# Revit family: PRD_AR_BbChngngUnts_CAMBRINOChangingTable_CAMB10HP_CAMB11HS
name_source: partatom
category: Specialty Equipment
revit_build: Autodesk Revit 2018 (Build: 20190510_1515(x64)
units: mm (PartAtom-declared; Revit-internal decimal feet)

## family parameters
Cut with Voids When Loaded = No
Host = Face
OmniClass Number = 23.40.20.21.37
OmniClass Title = Diaper Changing Units
Part Type = Normal
Room Calculation Point = No
Round Connector Dimension = Use Diameter
Shared = No

## types (2) — shared parameters
AssetType = Fixed
BodyMaterial = PRD_AR_SyntheticWhite
Category = Pr_40_20_76_06, Baby changing units
Color = white
Default Elevation = 900 mm  [stored 2.95276 ft]
DimensionsWhenClosed = 860 x 565 x 100 mm (W x H x D)
DimensionsWhenOpen = 860 x 480 x 570 mm (W x H x D)
DurationUnit = year
Finish = synthetic
Hinged = Yes
IfcExportAs = IfcFurnitureType
IfcExportType = USERDEFINED
IntegralAccessories = incl. mounting materials
IsBuiltIn = TRUE
MainColor = white
Manufacturer = KWC Group AG
ManufacturerName = KWC Group AG
ManufacturerURL = www.kwc.com
Material = synthetic
NBSDescription = Baby changing units
NBSReference = 45-35-72/316
NominalDepth = 100 mm  [stored 0.328084 ft]
NominalHeight = 565 mm  [stored 1.85367 ft]
NominalWidth = 860 mm  [stored 2.82152 ft]
ProductInformation = https://pim.kwc.com
Size = 860 x 565 x 100 mm (W x H x D)
Style = Changing table
TailorMade = No
TypeOfMounting = Wall mounting
URL = www.kwc.com
Uniclass2015Code = Pr_40_20_76_06
Uniclass2015Title = Baby changing units
Uniclass2015Version = Products v1.17
Version = 1
WarrantyDurationUnit = year

## per-type parameters (varying)
| type | BIMObjectName | Description | Features | GrossWeight | ModelNumber | Name | NetWeight | PanelMaterial |
| CAMB10HP | PRD_AR_BabyChangingUnits_CAMBRINOChangingTable_CAMB10HP | CAMBRINO horizontal baby changing table for wall mounting, made of polypropylene with antibacterial Biocote® protection, white colour, hinged, with integrated shock absorber for safe opening and closing, nylon safety belt and hooks on both sides, lockable dispenser for single-use paper covers in Interfold folding with maximum width 260 mm. Certified according to EN 12221-1 and EN 12221-2. Including mounting material and 80 single-use paper covers. | made of polypropylene with antibacterial Biocote® protection | 13.90 kg | 2030057691 | Changing Table CAMB10HP | 12.30 kg | PRD_AR_SyntheticWhite |
| CAMB11HS | PRD_AR_BabyChangingUnits_CAMBRINOChangingTable_CAMB11HS | CAMBRINO horizontal baby changing table for wall mounting, made of polypropylene with antibacterial Biocote® protection, white colour, front panel made of stainless steel, hinged, with integrated shock absorber for safe opening and closing, nylon safety belt and hooks on both sides, lockable dispenser for single-use paper covers in Interfold folding with maximum width 260 mm. Certified according to EN 12221-1 and EN 12221-2. Including mounting material and 80 single-use paper covers. | made of polypropylene with antibacterial Biocote® protection, front panel made of stainless steel | 17.60 kg | 2030057693 | Changing Table CAMB11HS | 16.00 kg | PRD_AR_StainlessSteel_SatinFinished |

note: column(s) folded — value = type name in every type: Model, ModelReference

note: [stored X ft] marks values corroborated as IEEE doubles in the binary element streams (Revit-internal decimal feet)

## geometry (parser evidence)
native form markers: Sweep x8
no freeform markers — native parametric forms only
